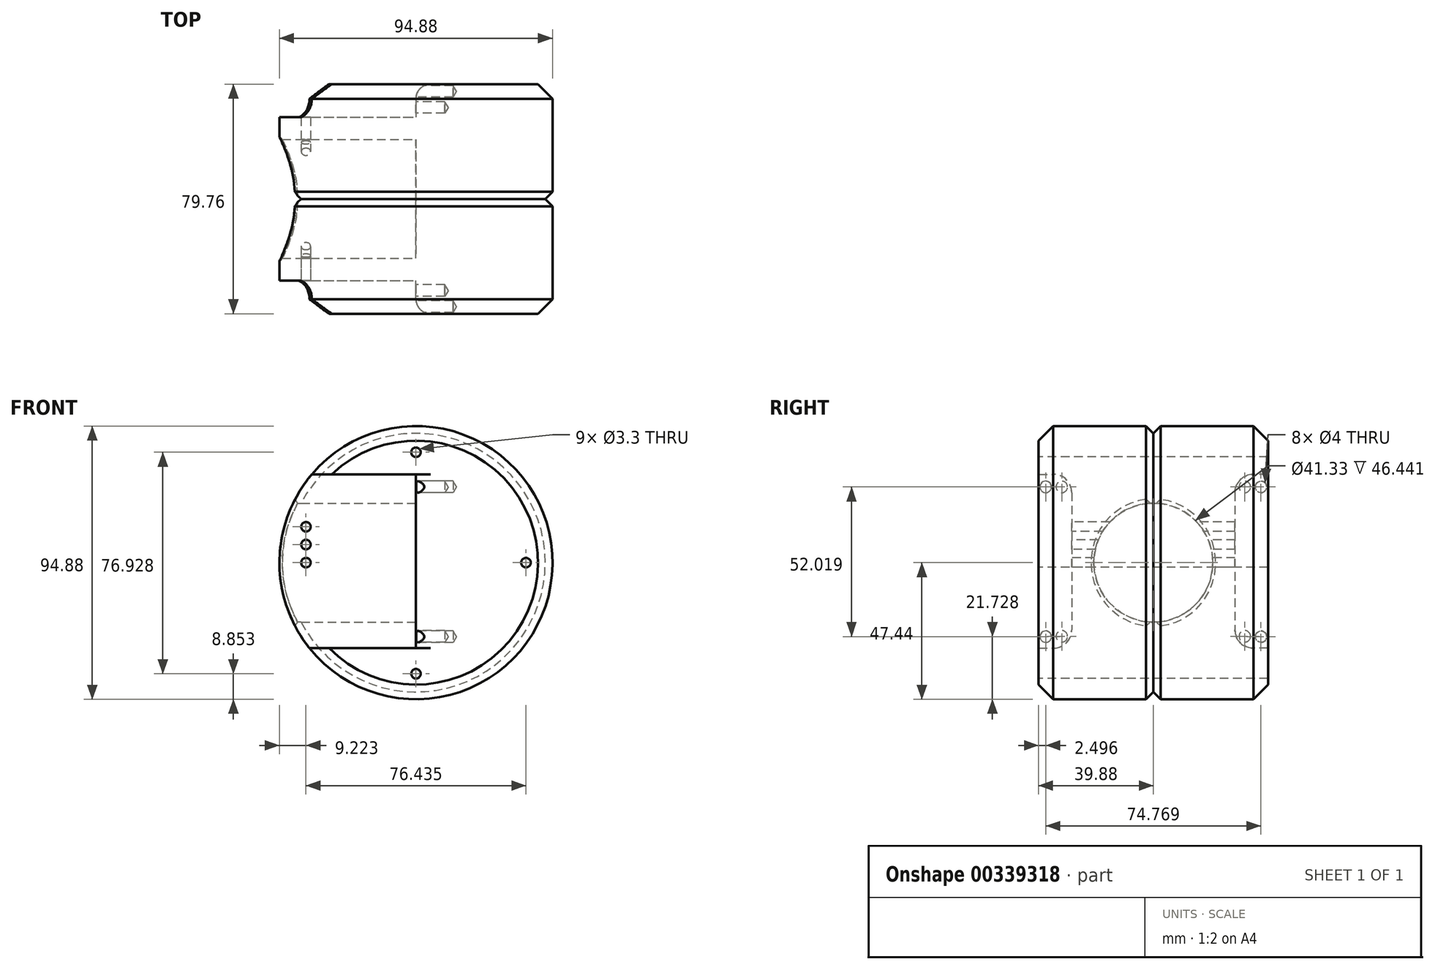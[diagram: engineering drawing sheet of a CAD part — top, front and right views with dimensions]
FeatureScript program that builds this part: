
annotation { "Feature Type Name" : "Feature", "Feature Type Description" : "" }
export const myFeature = defineFeature(function(context is Context, id is Id, definition is map)
    precondition{}
    {
        {
            var Q0;
            Q0=qCreatedBy(makeId("Front.planeOp"),FACE);
            var sketch = newSketch(context, id + "F0", { "sketchPlane" : qUnion([Q0])});
            skCircle(sketch, "E0", {"center": v(0, 0) * mm, "radius": 47.44 * mm});
            skSolve(sketch);
        }
        {
            var Q0;
            Q0=makeQuery(id+"F0.imprint","IMPRINT",FACE,{"disambiguationData":[TD([[makeQuery(id+"F0.imprint","IMPRINT",EDGE,{"derivedFrom":sQuery(id+"F0.wireOp",EDGE,"E0")}),1.0]])]});
            extrude(context, id + "F1", {"entities" : qUnion([Q0]), "depth" : 39.88 * mm});
        }
        {
            var Q0;
            Q0=makeQuery(id+"F1.opExtrude","CAP_EDGE",EDGE,{"disambiguationData":[OSD([sQuery(id+"F0.wireOp",EDGE,"E0")])],"isStart":false});
            chamfer(context, id + "F2", {"entities" : qUnion([Q0]), "width" : 5.08 * mm, "tangentPropagation" : true});
        }
        {
            var Q0;
            Q0=makeQuery(id+"F1.opExtrude","CAP_FACE",FACE,{"disambiguationData":[OSD([sQuery(id+"F0.wireOp",EDGE,"E0")])],"isStart":false});
            var sketch = newSketch(context, id + "F3", { "sketchPlane" : qUnion([Q0])});
            skPoint(sketch, "E1", {"position": v(0, 38.34) * mm});
            skPoint(sketch, "E2", {"position": v(38.22, 0) * mm});
            skPoint(sketch, "E3", {"position": v(0, -38.59) * mm});
            skPoint(sketch, "E4", {"position": v(-38.22, 0) * mm});
            skPoint(sketch, "E5", {"position": v(-38.22, 6.29) * mm});
            skPoint(sketch, "E6", {"position": v(-38.22, 12.45) * mm});
            skSolve(sketch);
        }
        {
            var Q0;
            Q0=sQuery(id+"F3.wireOp",VERTEX,"E4");
            var Q1;
            Q1=sQuery(id+"F3.wireOp",VERTEX,"E5");
            var Q2;
            Q2=sQuery(id+"F3.wireOp",VERTEX,"E6");
            var Q3;
            Q3=sQuery(id+"F3.wireOp",VERTEX,"E1");
            var Q4;
            Q4=sQuery(id+"F3.wireOp",VERTEX,"E2");
            var Q5;
            Q5=sQuery(id+"F3.wireOp",VERTEX,"E3");
            var Q6;
            Q6=makeQuery(id+"F1.opExtrude","SWEPT_BODY",BODY,{"disambiguationData":[OSD([sQuery(id+"F0.wireOp",EDGE,"E0")])]});
            hole(context, id + "F4", {"style" : HoleStyle.SIMPLE, "endStyle" : HoleEndStyle.THROUGH, "standardTappedOrClearance" : lookupTablePath({ "standard" : "ISO", "fit" : "Normal", "size" : "M3", "type" : "Clearance" }), "standardBlindInLast" : lookupTablePath({ "fit" : "Standard", "standard" : "ISO", "size" : "M3", "type" : "Clearance" }), "holeDiameter" : 3.3 * mm, "tappedDepth" : 12.7 * mm, "tapClearance" : 3, "locations" : qUnion([Q0, Q1, Q2, Q3, Q4, Q5]), "scope" : qUnion([Q6])});
        }
        {
            var Q0;
            Q0=qCreatedBy(makeId("Right.planeOp"),FACE);
            var sketch = newSketch(context, id + "F5", { "sketchPlane" : qUnion([Q0])});
            skLineSegment(sketch, "E7.bottom", {"start": v(-51.29, 30.7) * mm, "end": v(-34.7, 30.7) * mm});
            skLineSegment(sketch, "E7.top", {"start": v(-51.29, -29.71) * mm, "end": v(-34.7, -29.71) * mm});
            skLineSegment(sketch, "E7.left", {"start": v(-51.29, 30.7) * mm, "end": v(-51.29, -29.71) * mm});
            skLineSegment(sketch, "E7.right", {"start": v(-28.35, 24.35) * mm, "end": v(-28.35, -23.36) * mm});
            skPoint(sketch, "E8.visualSharp", {"position": v(-28.35, 30.7) * mm});
            skArc(sketch, "E8.filletArc", {"start": v(-28.35, 24.35) * mm, "mid": v(-30.21, 28.84) * mm, "end": v(-34.7, 30.7) * mm});
            skPoint(sketch, "E9.visualSharp", {"position": v(-28.35, -29.71) * mm});
            skArc(sketch, "E9.filletArc", {"start": v(-34.7, -29.71) * mm, "mid": v(-30.21, -27.85) * mm, "end": v(-28.35, -23.36) * mm});
            skSolve(sketch);
        }
        {
            var Q0;
            Q0=makeQuery(id+"F5.imprint","IMPRINT",FACE,{"disambiguationData":[TD([[makeQuery(id+"F5.imprint","IMPRINT",EDGE,{"derivedFrom":sQuery(id+"F5.wireOp",EDGE,"E7.bottom")}),-1.0]])]});
            extrude(context, id + "F6", {"entities" : qUnion([Q0]), "operationType" : NewBodyOperationType.REMOVE, "oppositeDirection" : true, "depth" : 52.83 * mm});
        }
        {
            var Q0;
            Q0=makeQuery(id+"F6.boolean.opBoolean","INTERSECT",EDGE,{"derivedFrom":[makeQuery(id+"F1.opExtrude","CAP_FACE",FACE,{"disambiguationData":[OSD([sQuery(id+"F0.wireOp",EDGE,"E0")])],"isStart":false}),makeQuery(id+"F6.opExtrude","CAP_FACE",FACE,{"disambiguationData":[OSD([sQuery(id+"F5.wireOp",EDGE,"E7.bottom"),sQuery(id+"F5.wireOp",EDGE,"E7.top"),sQuery(id+"F5.wireOp",EDGE,"E7.left"),sQuery(id+"F5.wireOp",EDGE,"E7.right"),sQuery(id+"F5.wireOp",EDGE,"E8.filletArc"),sQuery(id+"F5.wireOp",EDGE,"E9.filletArc")])],"isStart":true})]});
            fillet(context, id + "F7", {"entities" : qUnion([Q0]), "radius" : 5.08 * mm, "tangentPropagation" : true, "allowEdgeOverflow" : false});
        }
        {
            var Q0;
            Q0=makeQuery(id+"F6.boolean.opBoolean","COPY",FACE,{"derivedFrom":makeQuery(id+"F6.opExtrude","CAP_FACE",FACE,{"disambiguationData":[OSD([sQuery(id+"F5.wireOp",EDGE,"E7.bottom"),sQuery(id+"F5.wireOp",EDGE,"E7.top"),sQuery(id+"F5.wireOp",EDGE,"E7.left"),sQuery(id+"F5.wireOp",EDGE,"E7.right"),sQuery(id+"F5.wireOp",EDGE,"E8.filletArc"),sQuery(id+"F5.wireOp",EDGE,"E9.filletArc")])],"isStart":true})});
            var sketch = newSketch(context, id + "F8", { "sketchPlane" : qUnion([Q0])});
            skPoint(sketch, "E10", {"position": v(31.8, 26.3) * mm});
            skPoint(sketch, "E11", {"position": v(37.38, 26.3) * mm});
            skPoint(sketch, "E12", {"position": v(31.8, -25.58) * mm});
            skPoint(sketch, "E13", {"position": v(37.38, -25.71) * mm});
            skSolve(sketch);
        }
        {
            var Q0;
            Q0=sQuery(id+"F8.wireOp",VERTEX,"E10");
            var Q1;
            Q1=sQuery(id+"F8.wireOp",VERTEX,"E11");
            var Q2;
            Q2=sQuery(id+"F8.wireOp",VERTEX,"E12");
            var Q3;
            Q3=sQuery(id+"F8.wireOp",VERTEX,"E13");
            var Q4;
            Q4=makeQuery(id+"F1.opExtrude","SWEPT_BODY",BODY,{"disambiguationData":[OSD([sQuery(id+"F0.wireOp",EDGE,"E0")])]});
            hole(context, id + "F9", {"style" : HoleStyle.SIMPLE, "endStyle" : HoleEndStyle.BLIND, "holeDiameter" : 4 * mm, "holeDepth" : 10 * mm, "tappedDepth" : 12.7 * mm, "tapClearance" : 3, "locations" : qUnion([Q0, Q1, Q2, Q3]), "scope" : qUnion([Q4])});
        }
        {
            var Q0;
            Q0=makeQuery(id+"F1.opExtrude","CAP_EDGE",EDGE,{"disambiguationData":[OSD([sQuery(id+"F0.wireOp",EDGE,"E0")])],"isStart":true});
            chamfer(context, id + "F10", {"entities" : qUnion([Q0]), "width" : 2.54 * mm, "tangentPropagation" : true});
        }
        {
            var Q0;
            Q0=makeQuery(id+"F1.opExtrude","SWEPT_BODY",BODY,{"disambiguationData":[OSD([sQuery(id+"F0.wireOp",EDGE,"E0")])]});
            var Q1;
            Q1=qCreatedBy(makeId("Front.planeOp"),FACE);
            mirror(context, id + "F11", {"operationType" : NewBodyOperationType.ADD, "entities" : qUnion([Q0]), "mirrorPlane" : qUnion([Q1])});
        }
        {
            var Q0;
            Q0=qCreatedBy(makeId("Right.planeOp"),FACE);
            var sketch = newSketch(context, id + "F12", { "sketchPlane" : qUnion([Q0])});
            skCircle(sketch, "E14", {"center": v(0, 0) * mm, "radius": 20.66 * mm});
            skSolve(sketch);
        }
        {
            var Q0;
            Q0 = qSketchRegion(id + "F12", true);
            extrude(context, id + "F13", {"entities" : qUnion([Q0]), "operationType" : NewBodyOperationType.REMOVE, "oppositeDirection" : true, "depth" : 97.03 * mm});
        }
        {
            var Q0;
            Q0=makeQuery(id+"F13.boolean.opBoolean","INTERSECT",EDGE,{"derivedFrom":[makeQuery(id+"F11.opPattern","COPY",FACE,{"derivedFrom":makeQuery(id+"F1.opExtrude","SWEPT_FACE",FACE,{"disambiguationData":[OSD([sQuery(id+"F0.wireOp",EDGE,"E0")])]}),"instanceName":"1"}),makeQuery(id+"F13.opExtrude","SWEPT_FACE",FACE,{"disambiguationData":[OSD([sQuery(id+"F12.wireOp",EDGE,"E14")])]})]});
            var Q1;
            Q1=makeQuery(id+"F13.boolean.opBoolean","INTERSECT",EDGE,{"derivedFrom":[makeQuery(id+"F1.opExtrude","SWEPT_FACE",FACE,{"disambiguationData":[OSD([sQuery(id+"F0.wireOp",EDGE,"E0")])]}),makeQuery(id+"F13.opExtrude","SWEPT_FACE",FACE,{"disambiguationData":[OSD([sQuery(id+"F12.wireOp",EDGE,"E14")])]})]});
            chamfer(context, id + "F14", {"entities" : qUnion([Q0, Q1]), "width" : 1 * mm, "tangentPropagation" : true});
        }
    });
